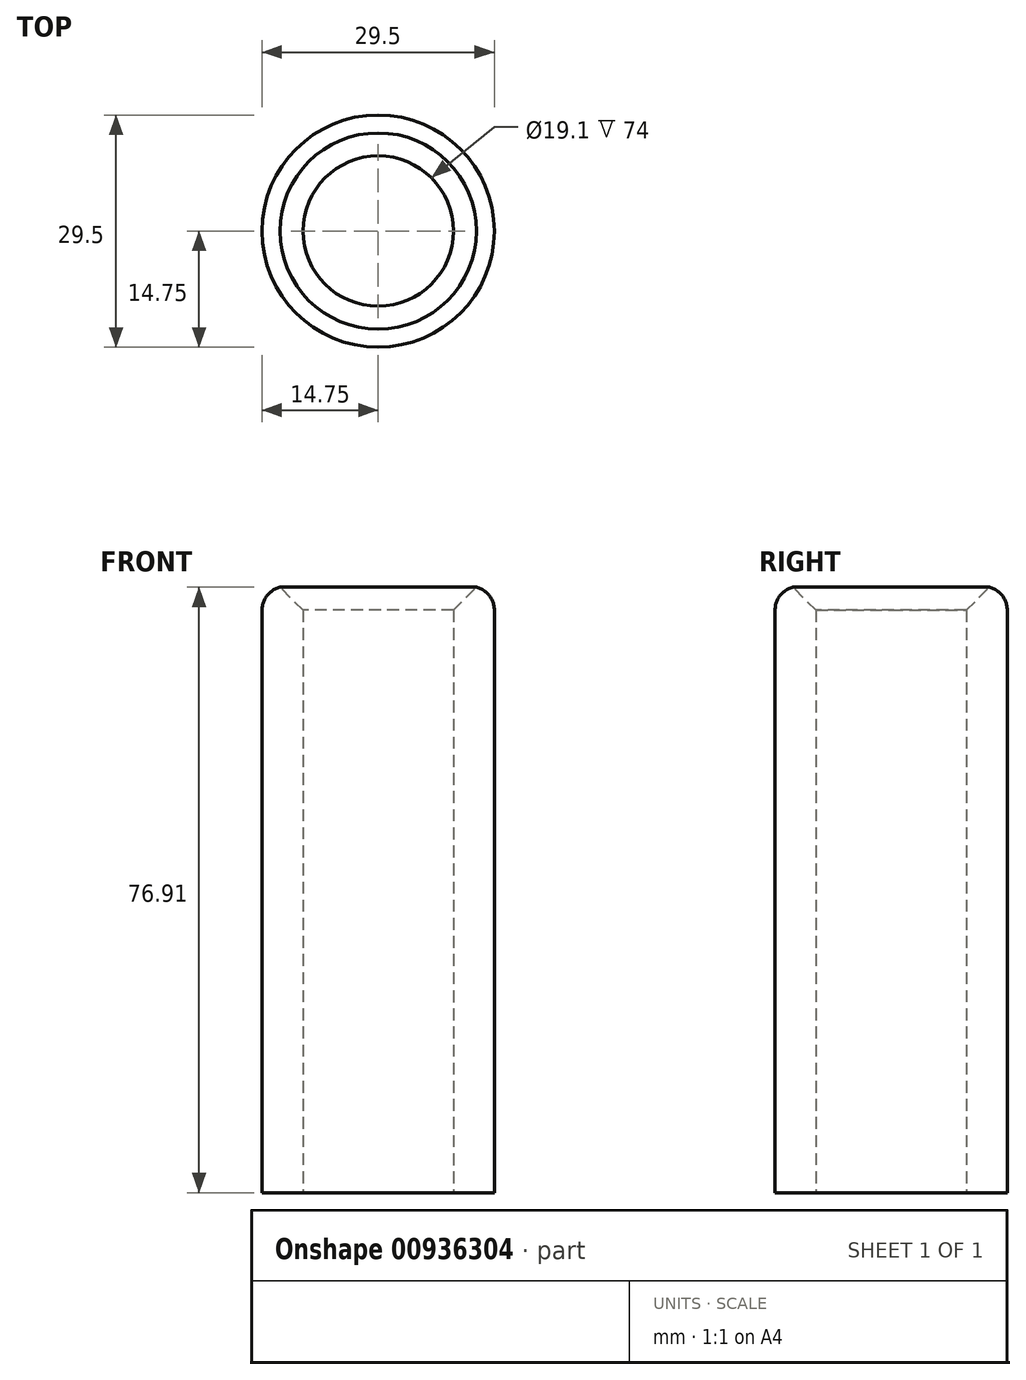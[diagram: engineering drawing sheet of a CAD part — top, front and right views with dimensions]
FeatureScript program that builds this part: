
annotation { "Feature Type Name" : "Feature", "Feature Type Description" : "" }
export const myFeature = defineFeature(function(context is Context, id is Id, definition is map)
    precondition{}
    {
        {
            var Q0;
            Q0=qCreatedBy(makeId("Top.planeOp"),FACE);
            var sketch = newSketch(context, id + "F0", { "sketchPlane" : qUnion([Q0])});
            skCircle(sketch, "E0", {"center": v(0, 0) * mm, "radius": 14.75 * mm});
            skSolve(sketch);
        }
        {
            var Q0;
            Q0=makeQuery(id+"F0.imprint","IMPRINT",FACE,{"disambiguationData":[TD([[makeQuery(id+"F0.imprint","IMPRINT",EDGE,{"derivedFrom":sQuery(id+"F0.wireOp",EDGE,"E0")}),1.0]])]});
            extrude(context, id + "F1", {"entities" : qUnion([Q0]), "depth" : 77 * mm, "offsetDistance" : 25 * mm});
        }
        {
            var Q0;
            Q0=qCreatedBy(makeId("Top.planeOp"),FACE);
            var sketch = newSketch(context, id + "F2", { "sketchPlane" : qUnion([Q0])});
            skCircle(sketch, "E1", {"center": v(0, 0) * mm, "radius": 9.55 * mm});
            skSolve(sketch);
        }
        {
            var Q0;
            Q0 = qSketchRegion(id + "F2", true);
            extrude(context, id + "F3", {"entities" : qUnion([Q0]), "operationType" : NewBodyOperationType.REMOVE, "endBound" : BoundingType.THROUGH_ALL, "depth" : 77 * mm, "offsetDistance" : 25 * mm});
        }
        {
            var Q0;
            Q0=makeQuery(id+"F1.opExtrude","CAP_EDGE",EDGE,{"disambiguationData":[OSD([sQuery(id+"F0.wireOp",EDGE,"E0")])],"isStart":false});
            fillet(context, id + "F4", {"entities" : qUnion([Q0]), "radius" : 3 * mm, "tangentPropagation" : true, "allowEdgeOverflow" : false});
        }
        {
            var Q0;
            Q0=makeQuery(id+"F3.boolean.opBoolean","INTERSECT",EDGE,{"derivedFrom":[makeQuery(id+"F1.opExtrude","CAP_FACE",FACE,{"disambiguationData":[OSD([sQuery(id+"F0.wireOp",EDGE,"E0")])],"isStart":false}),makeQuery(id+"F3.opExtrude","SWEPT_FACE",FACE,{"disambiguationData":[OSD([sQuery(id+"F2.wireOp",EDGE,"E1")])]})]});
            chamfer(context, id + "F5", {"entities" : qUnion([Q0]), "width" : 3 * mm, "tangentPropagation" : true});
        }
    });
